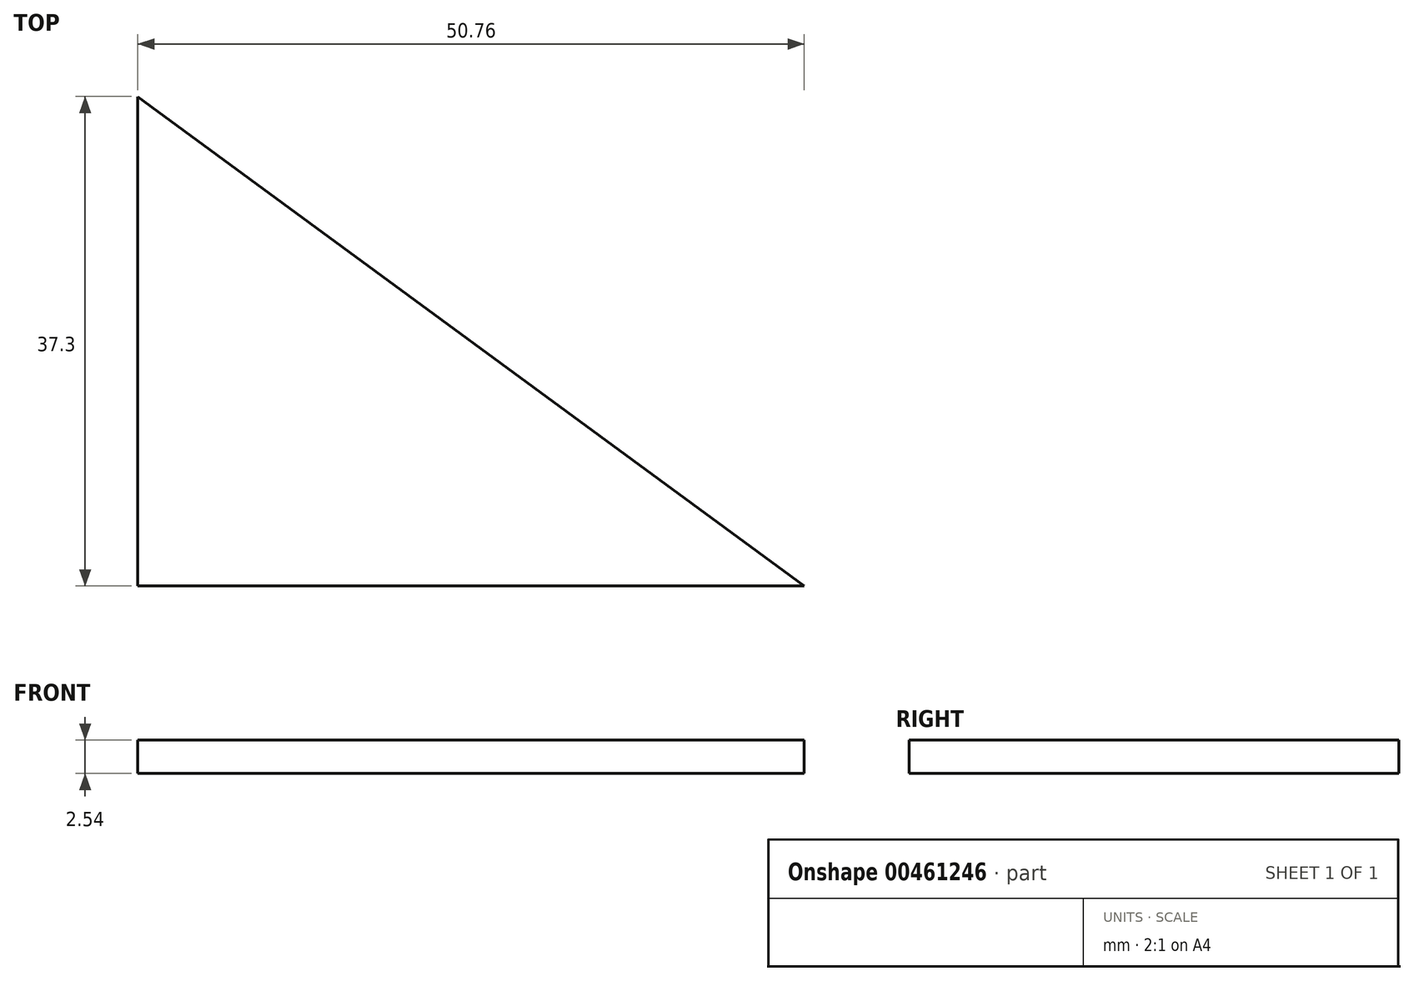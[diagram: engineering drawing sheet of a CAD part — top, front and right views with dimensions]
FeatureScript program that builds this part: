
annotation { "Feature Type Name" : "Feature", "Feature Type Description" : "" }
export const myFeature = defineFeature(function(context is Context, id is Id, definition is map)
    precondition{}
    {
        {
            var Q0;
            Q0=qCreatedBy(makeId("Top.planeOp"),FACE);
            var sketch = newSketch(context, id + "F0", { "sketchPlane" : qUnion([Q0])});
            skLineSegment(sketch, "E0", {"start": v(-50.76, 37.3) * mm, "end": v(-50.76, 0) * mm});
            skLineSegment(sketch, "E1", {"start": v(-50.76, 0) * mm, "end": v(0, 0) * mm});
            skLineSegment(sketch, "E2", {"start": v(0, 0) * mm, "end": v(-50.76, 37.3) * mm});
            skSolve(sketch);
        }
        {
            var Q0;
            Q0=qSketchRegion(id+"F0",true);
            extrude(context, id + "F1", {"entities" : qUnion([Q0]), "depth" : 2.54 * mm});
        }
    });
